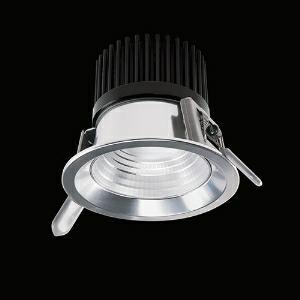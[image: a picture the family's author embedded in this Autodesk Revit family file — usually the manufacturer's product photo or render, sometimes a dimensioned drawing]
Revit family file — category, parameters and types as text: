
# Revit family: spectral_myral_myral_4500-830-f
name_source: partatom
category: Lighting Fixtures
revit_build: Autodesk Revit 2016 (Build: 20150220_1215(x64)
units: mm (PartAtom-declared; Revit-internal decimal feet)

## family parameters
Cut with Voids When Loaded = No
Host = Face
Light Source = No
Part Type = Normal
Room Calculation Point = No
Round Connector Dimension = Use Diameter
Shared = No

## types (1)
- SPECTRAL MYRAL (1 x )
    Apparent Load = 0 VA
    Approval mark = CE
    CIE Flux Codes = 81 99 100 100 100
    Control Gear = Electronic transformer
    Default Elevation = 1800 mm
    Description = SPG0320188
MYRAL recessed spot

Design:
    Height = 0 mm  [stored 0 ft]
    Lamp = 1 x
    Lamp count = 1
    Length = 120 mm
    Luminous efficacy = 0 lm/W
    Manufacturer = Ridi
    ModVariant = No
    Model = MYRAL 4500-830-F
    Mounting Place = Ceiling
    Mounting Type = Recessed
    Number of Poles = 1
    OnlyDefault = Yes
    Power Factor = 1
    Product Name = SPECTRAL MYRAL
    Product group = Downlight recessed
    ProductGroupID = 400
    Protection Class = Protection class
    Protection Degree = IP 20
    RlxData = <blob elided: 38885 chars, md5=5eb86771>
    Socket = socket
    Standby Power = 0 W
    System Light Flux = 0 lm
    System Power = 0 W
    Type Image = myral_04.jpg
    URL = http://reluxnet.relux.com
    VarID = ---
    Voltage = 0 V
    Weight = 0.00 kg
    Width = 0 mm  [stored 0 ft]

note: [stored X ft] marks values corroborated as IEEE doubles in the binary element streams (Revit-internal decimal feet)

## geometry (parser evidence)
native form markers: Sweep x11
no freeform markers — native parametric forms only
